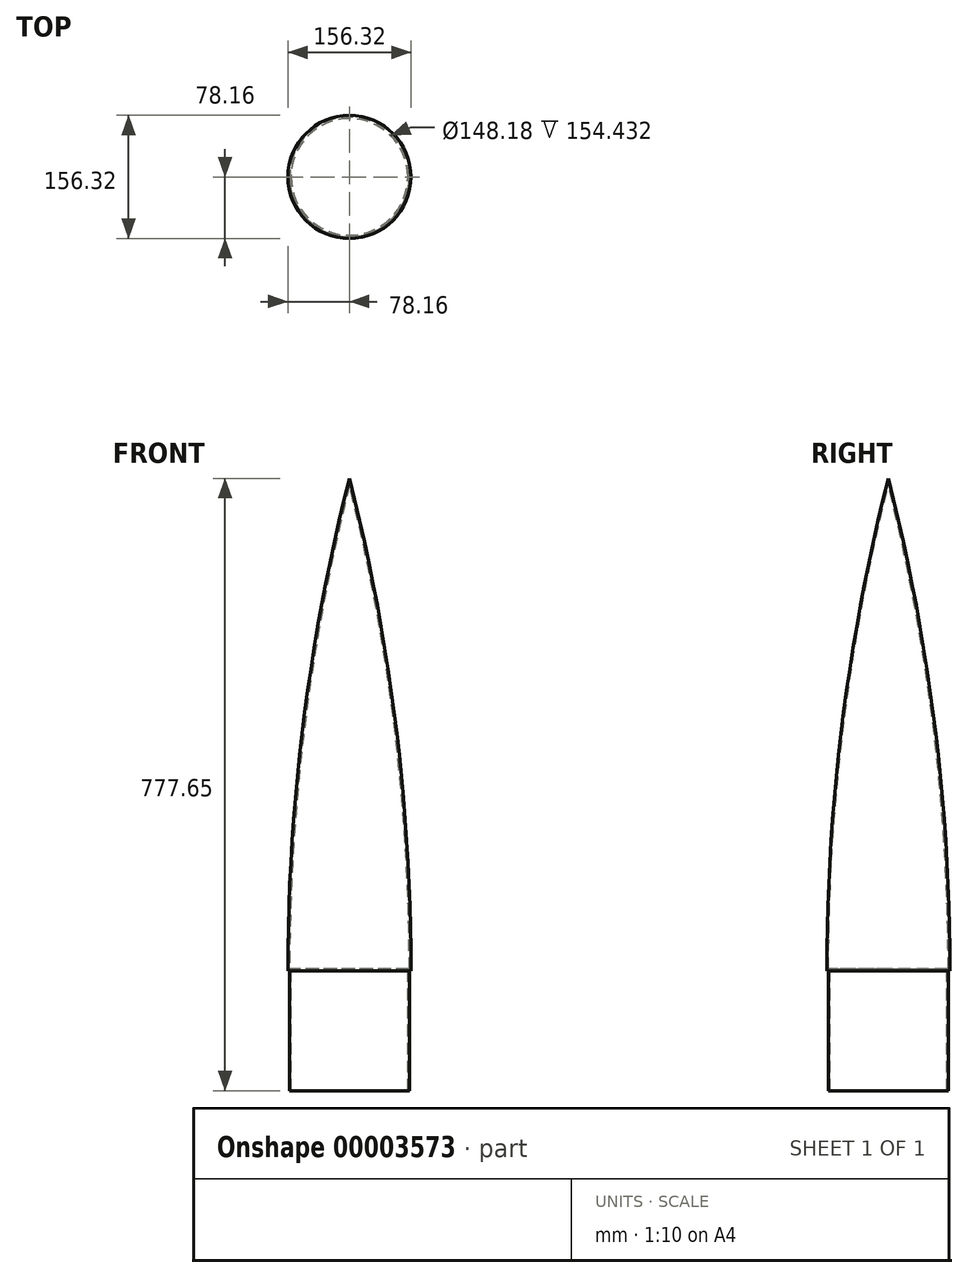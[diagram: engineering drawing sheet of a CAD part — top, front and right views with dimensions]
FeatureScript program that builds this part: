
annotation { "Feature Type Name" : "Feature", "Feature Type Description" : "" }
export const myFeature = defineFeature(function(context is Context, id is Id, definition is map)
    precondition{}
    {
        {
            var Q0;
            Q0=qCreatedBy(makeId("Front.planeOp"),FACE);
            var sketch = newSketch(context, id + "F0", { "sketchPlane" : qUnion([Q0])});
            skLineSegment(sketch, "E0", {"start": v(0, -152.4) * mm, "end": v(76.12, -152.4) * mm});
            skLineSegment(sketch, "E1", {"start": v(76.12, -152.4) * mm, "end": v(76.12, 0) * mm});
            skLineSegment(sketch, "E2", {"start": v(76.12, 0) * mm, "end": v(78.16, 0) * mm});
            skArc(sketch, "E3", {"start": v(78.16, 0) * mm, "mid": v(58.54, 315.06) * mm, "end": v(0, 625.25) * mm});
            skLineSegment(sketch, "E4", {"start": v(0, 625.25) * mm, "end": v(0, -152.4) * mm, "construction": true});
            skLineSegment(sketch, "E5", {"start": v(78.16, 0) * mm, "end": v(78.16, 625.25) * mm, "construction": true});
            skLineSegment(sketch, "E6", {"start": v(0, 625.25) * mm, "end": v(0, -152.4) * mm});
            skLineSegment(sketch, "E7", {"start": v(0, -118.57) * mm, "end": v(0, -255.66) * mm, "construction": true});
            skSolve(sketch);
        }
        {
            var Q0;
            Q0 = qSketchRegion(id + "F0", true);
            var Q1;
            Q1=sQuery(id+"F0.wireOp",EDGE,"E7");
            var Q2;
            Q2=sQuery(id+"F0.wireOp",EDGE,"E6");
            revolve(context, id + "F1", {"entities" : qUnion([Q0]), "surfaceEntities" : qUnion([Q1]), "axis" : qUnion([Q2]), "revolveType" : RevolveType.FULL});
        }
        {
            var Q0;
            Q0=makeQuery(id+"F1.opRevolve","SWEPT_FACE",FACE,{"disambiguationData":[OSD([sQuery(id+"F0.wireOp",EDGE,"E0")])]});
            shell(context, id + "F2", {"entities" : qUnion([Q0]), "thickness" : 2.03 * mm});
        }
    });
